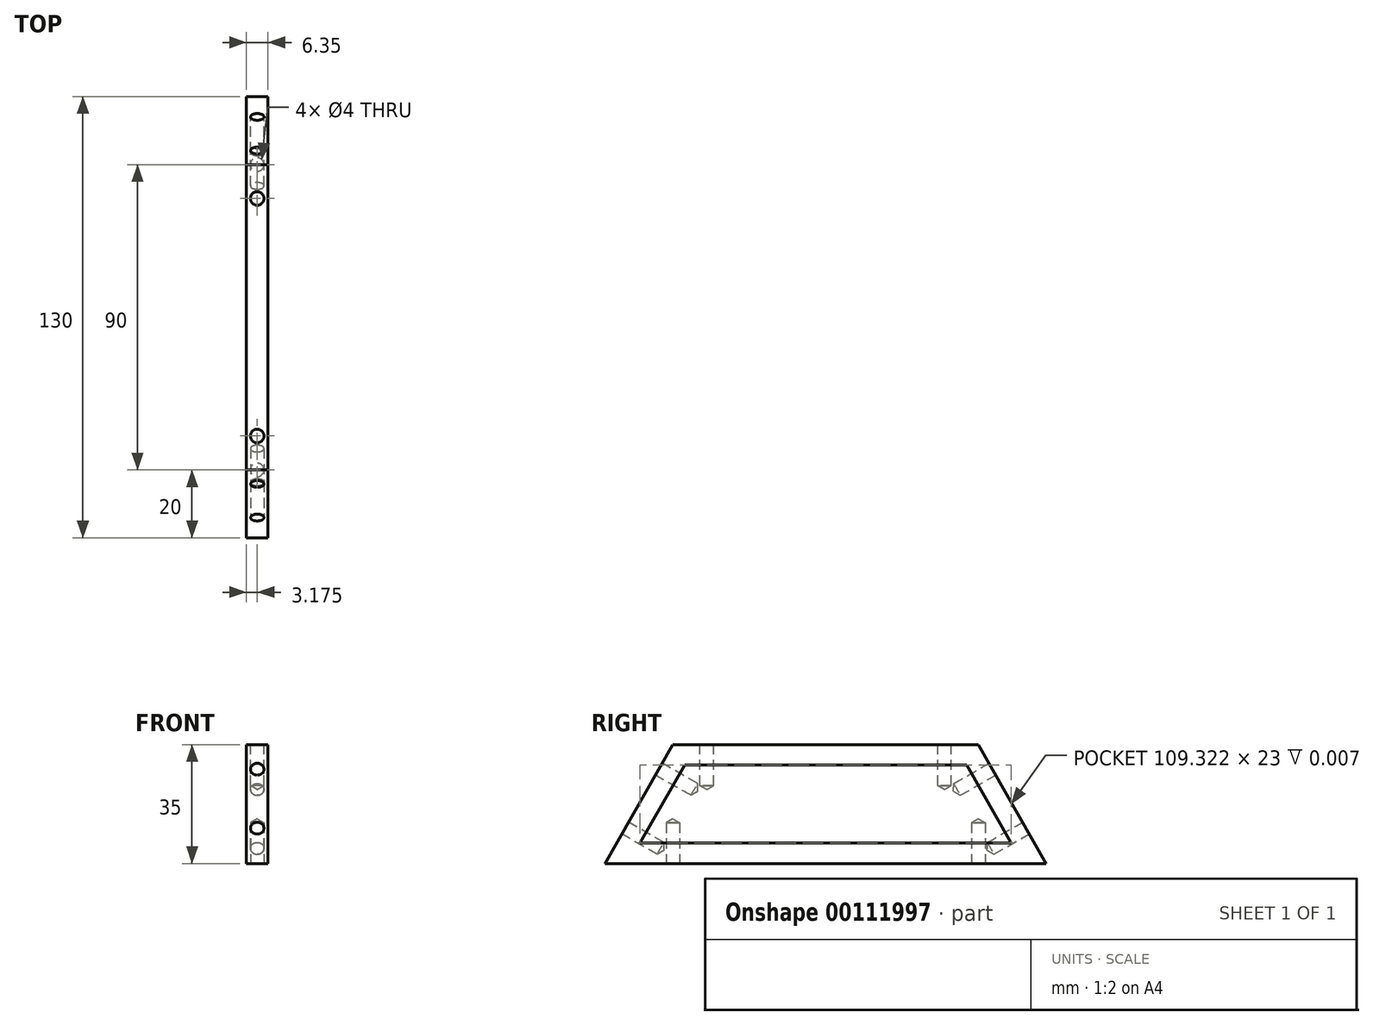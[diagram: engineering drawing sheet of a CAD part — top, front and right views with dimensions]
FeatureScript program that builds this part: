
annotation { "Feature Type Name" : "Feature", "Feature Type Description" : "" }
export const myFeature = defineFeature(function(context is Context, id is Id, definition is map)
    precondition{}
    {
        {
            var Q0;
            Q0=qCreatedBy(makeId("Right.planeOp"),FACE);
            var sketch = newSketch(context, id + "F0", { "sketchPlane" : qUnion([Q0])});
            skLineSegment(sketch, "E0", {"start": v(0, 0) * mm, "end": v(20, 35) * mm});
            skLineSegment(sketch, "E1", {"start": v(20, 35) * mm, "end": v(110, 35) * mm});
            skLineSegment(sketch, "E2", {"start": v(110, 35) * mm, "end": v(130, 0) * mm});
            skLineSegment(sketch, "E3", {"start": v(130, 0) * mm, "end": v(0, 0) * mm});
            skSolve(sketch);
        }
        {
            var Q0;
            Q0 = qSketchRegion(id + "F0", true);
            extrude(context, id + "F1", {"entities" : qUnion([Q0]), "depth" : 6.35 * mm});
        }
        {
            var Q0;
            Q0=makeQuery(id+"F1.opExtrude","CAP_FACE",FACE,{"disambiguationData":[OSD([sQuery(id+"F0.wireOp",EDGE,"E0"),sQuery(id+"F0.wireOp",EDGE,"E1"),sQuery(id+"F0.wireOp",EDGE,"E2"),sQuery(id+"F0.wireOp",EDGE,"E3")])],"isStart":false});
            var sketch = newSketch(context, id + "F2", { "sketchPlane" : qUnion([Q0])});
            skLineSegment(sketch, "E4.0", {"start": v(10.34, 6) * mm, "end": v(23.48, 29) * mm});
            skLineSegment(sketch, "E4.1", {"start": v(119.66, 6) * mm, "end": v(10.34, 6) * mm});
            skLineSegment(sketch, "E4.2", {"start": v(106.52, 29) * mm, "end": v(119.66, 6) * mm});
            skLineSegment(sketch, "E4.3", {"start": v(23.48, 29) * mm, "end": v(106.52, 29) * mm});
            skSolve(sketch);
        }
        {
            var Q0;
            Q0 = qSketchRegion(id + "F2", true);
            extrude(context, id + "F3", {"entities" : qUnion([Q0]), "operationType" : NewBodyOperationType.REMOVE, "oppositeDirection" : true, "depth" : 3 / 406.4 * mm});
        }
        {
            var Q0;
            Q0=makeQuery(id+"F1.opExtrude","SWEPT_FACE",FACE,{"disambiguationData":[OSD([sQuery(id+"F0.wireOp",EDGE,"E3")])]});
            var sketch = newSketch(context, id + "F4", { "sketchPlane" : qUnion([Q0])});
            skPoint(sketch, "E5", {"position": v(3.18, -110) * mm});
            skPoint(sketch, "E6", {"position": v(3.18, -20) * mm});
            skPoint(sketch, "E7", {"position": v(3.17, 0) * mm});
            skSolve(sketch);
        }
        {
            var Q0;
            Q0=makeQuery(id+"F1.opExtrude","SWEPT_FACE",FACE,{"disambiguationData":[OSD([sQuery(id+"F0.wireOp",EDGE,"E1")])]});
            var sketch = newSketch(context, id + "F5", { "sketchPlane" : qUnion([Q0])});
            skPoint(sketch, "E8", {"position": v(3.17, 110) * mm});
            skPoint(sketch, "E9", {"position": v(3.18, 100) * mm});
            skPoint(sketch, "E10", {"position": v(3.18, 30) * mm});
            skSolve(sketch);
        }
        {
            var Q0;
            Q0=sQuery(id+"F4.wireOp",VERTEX,"E5");
            var Q1;
            Q1=sQuery(id+"F4.wireOp",VERTEX,"E6");
            var Q2;
            Q2=sQuery(id+"F5.wireOp",VERTEX,"E9");
            var Q3;
            Q3=sQuery(id+"F5.wireOp",VERTEX,"E10");
            var Q4;
            Q4=makeQuery(id+"F1.opExtrude","SWEPT_BODY",BODY,{"disambiguationData":[OSD([sQuery(id+"F0.wireOp",EDGE,"E0"),sQuery(id+"F0.wireOp",EDGE,"E1"),sQuery(id+"F0.wireOp",EDGE,"E2"),sQuery(id+"F0.wireOp",EDGE,"E3")])]});
            hole(context, id + "F6", {"style" : HoleStyle.SIMPLE, "endStyle" : HoleEndStyle.BLIND, "holeDiameter" : 4 * mm, "holeDepth" : 12 * mm, "locations" : qUnion([Q0, Q1, Q2, Q3]), "scope" : qUnion([Q4])});
        }
        {
            var Q0;
            Q0=makeQuery(id+"F1.opExtrude","SWEPT_FACE",FACE,{"disambiguationData":[OSD([sQuery(id+"F0.wireOp",EDGE,"E0")])]});
            var sketch = newSketch(context, id + "F7", { "sketchPlane" : qUnion([Q0])});
            skPoint(sketch, "E11", {"position": v(3.17, 0) * mm});
            skPoint(sketch, "E12", {"position": v(3.17, 12) * mm});
            skPoint(sketch, "E13", {"position": v(3.17, 32) * mm});
            skSolve(sketch);
        }
        {
            var Q0;
            Q0=makeQuery(id+"F1.opExtrude","SWEPT_FACE",FACE,{"disambiguationData":[OSD([sQuery(id+"F0.wireOp",EDGE,"E2")])]});
            var sketch = newSketch(context, id + "F8", { "sketchPlane" : qUnion([Q0])});
            skPoint(sketch, "E14", {"position": v(-3.17, -64.5) * mm});
            skPoint(sketch, "E15", {"position": v(-3.18, -52.5) * mm});
            skPoint(sketch, "E16", {"position": v(-3.18, -32.5) * mm});
            skSolve(sketch);
        }
        {
            var Q0;
            Q0=sQuery(id+"F8.wireOp",VERTEX,"E16");
            var Q1;
            Q1=sQuery(id+"F8.wireOp",VERTEX,"E15");
            var Q2;
            Q2=sQuery(id+"F7.wireOp",VERTEX,"E13");
            var Q3;
            Q3=sQuery(id+"F7.wireOp",VERTEX,"E12");
            var Q4;
            Q4=makeQuery(id+"F1.opExtrude","SWEPT_BODY",BODY,{"disambiguationData":[OSD([sQuery(id+"F0.wireOp",EDGE,"E0"),sQuery(id+"F0.wireOp",EDGE,"E1"),sQuery(id+"F0.wireOp",EDGE,"E2"),sQuery(id+"F0.wireOp",EDGE,"E3")])]});
            hole(context, id + "F9", {"style" : HoleStyle.SIMPLE, "endStyle" : HoleEndStyle.BLIND, "holeDiameter" : 4 * mm, "holeDepth" : 12 * mm, "locations" : qUnion([Q0, Q1, Q2, Q3]), "scope" : qUnion([Q4])});
        }
    });
